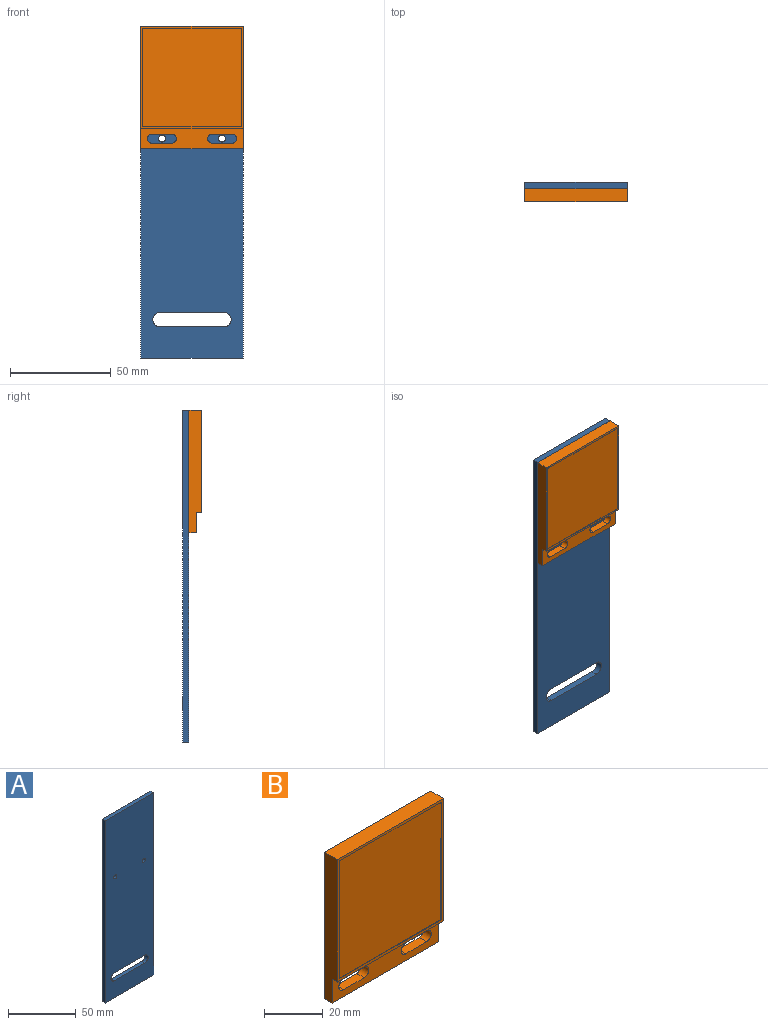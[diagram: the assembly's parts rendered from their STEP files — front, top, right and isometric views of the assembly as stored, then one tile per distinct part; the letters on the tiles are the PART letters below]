
ASSEMBLY  parts=2 mates=1
PART A: 12 faces, bbox 50.8x3.2x165.1 mm
  f0: plane 165.1x50.8mm, normal (0,-1,0), area 8101.7mm2, adj f2,f3,f4,f5,f6,f7,f8,f9
  f1: plane 165.1x50.8mm, normal (0,1,0), area 8101.7mm2, adj f2,f3,f4,f5,f6,f7,f8,f9
  f2: plane 165.1x3.18mm, normal (-1,0,0), area 524.2mm2, adj f0,f1,f4,f5
  f3: plane 165.1x3.18mm, normal (1,0,0), area 524.2mm2, adj f0,f1,f4,f5
  f4: plane 50.8x3.18mm, normal (0,0,1), area 161.3mm2, adj f0,f1,f2,f3
  f5: plane 50.8x3.18mm, normal (0,0,-1), area 161.3mm2, adj f0,f1,f2,f3
  f6: cylinder r=1.73mm len=3.45mm, axis (0,-1,0), area 34.5mm2, adj f0,f1
  f7: cylinder r=1.73mm len=3.45mm, axis (0,-1,0), area 34.5mm2, adj f0,f1
  f8: cylinder r=3.57mm len=7.14mm, axis (0,-1,0), area 35.6mm2, adj f0,f1,f9,f11
  f9: plane 31.75x3.18mm, normal (0,0,1), area 100.8mm2, adj f0,f1,f8,f10
  f10: cylinder r=3.57mm len=7.14mm, axis (0,-1,0), area 35.6mm2, adj f0,f1,f9,f11
  f11: plane 31.75x3.18mm, normal (0,0,-1), area 100.8mm2, adj f0,f1,f8,f10
PART B: 21 faces, bbox 51x6.2x61 mm
  f0: plane 61x51mm, normal (0,1,0), area 2989.2mm2, adj f1,f2,f3,f12,f13,f14,f15,f16
  f1: plane 61x6.2mm, normal (-1,0,0), area 352.2mm2, adj f0,f2,f4,f5,f6,f12
  f2: plane 51x6.2mm, normal (0,0,1), area 316.2mm2, adj f0,f1,f3,f6
  f3: plane 61x6.2mm, normal (1,0,0), area 352.2mm2, adj f0,f2,f4,f5,f6,f12
  f4: plane 51x10mm, normal (0,-1,0), area 388.2mm2, adj f1,f3,f5,f12,f13,f14,f15,f16
  f5: plane 51x2.6mm, normal (0,0,-1), area 132.6mm2, adj f1,f3,f4,f6
  f6: plane 51x51mm, normal (0,-1,0), area 200mm2, adj f1,f2,f3,f5,f7,f8,f9,f10
  f7: plane 49x0.2mm, normal (1,0,0), area 9.8mm2, adj f6,f8,f10,f11
  f8: plane 49x0.2mm, normal (0,0,-1), area 9.8mm2, adj f6,f7,f9,f11
  f9: plane 49x0.2mm, normal (-1,0,0), area 9.8mm2, adj f6,f8,f10,f11
  f10: plane 49x0.2mm, normal (0,0,1), area 9.8mm2, adj f6,f7,f9,f11
  f11: plane 49x49mm, normal (0,-1,0), area 2401mm2, adj f7,f8,f9,f10
  f12: plane 51x3.6mm, normal (0,0,-1), area 183.6mm2, adj f0,f1,f3,f4
  f13: cylinder r=2.25mm len=4.5mm, axis (0,-1,0), area 25.4mm2, adj f0,f4,f14,f16
  f14: plane 10x3.6mm, normal (0,0,-1), area 36mm2, adj f0,f4,f13,f15
  f15: cylinder r=2.25mm len=4.5mm, axis (0,-1,0), area 25.4mm2, adj f0,f4,f14,f16
  f16: plane 10x3.6mm, normal (0,0,1), area 36mm2, adj f0,f4,f13,f15
  f17: plane 10x3.6mm, normal (0,0,-1), area 36mm2, adj f0,f4,f18,f20
  f18: cylinder r=2.25mm len=4.5mm, axis (0,-1,0), area 25.4mm2, adj f0,f4,f17,f19
  f19: plane 10x3.6mm, normal (0,0,1), area 36mm2, adj f0,f4,f18,f20
  f20: cylinder r=2.25mm len=4.5mm, axis (0,-1,0), area 25.4mm2, adj f0,f4,f17,f19
PLACE A t=(-34.38,24.96,-24.26)mm
PLACE B t=(-32.9,18.28,110.34)mm
MATE fastened B.f0 <-> A.f0  axis (0,1,0) through (-32.9,18.28,140.84)mm
